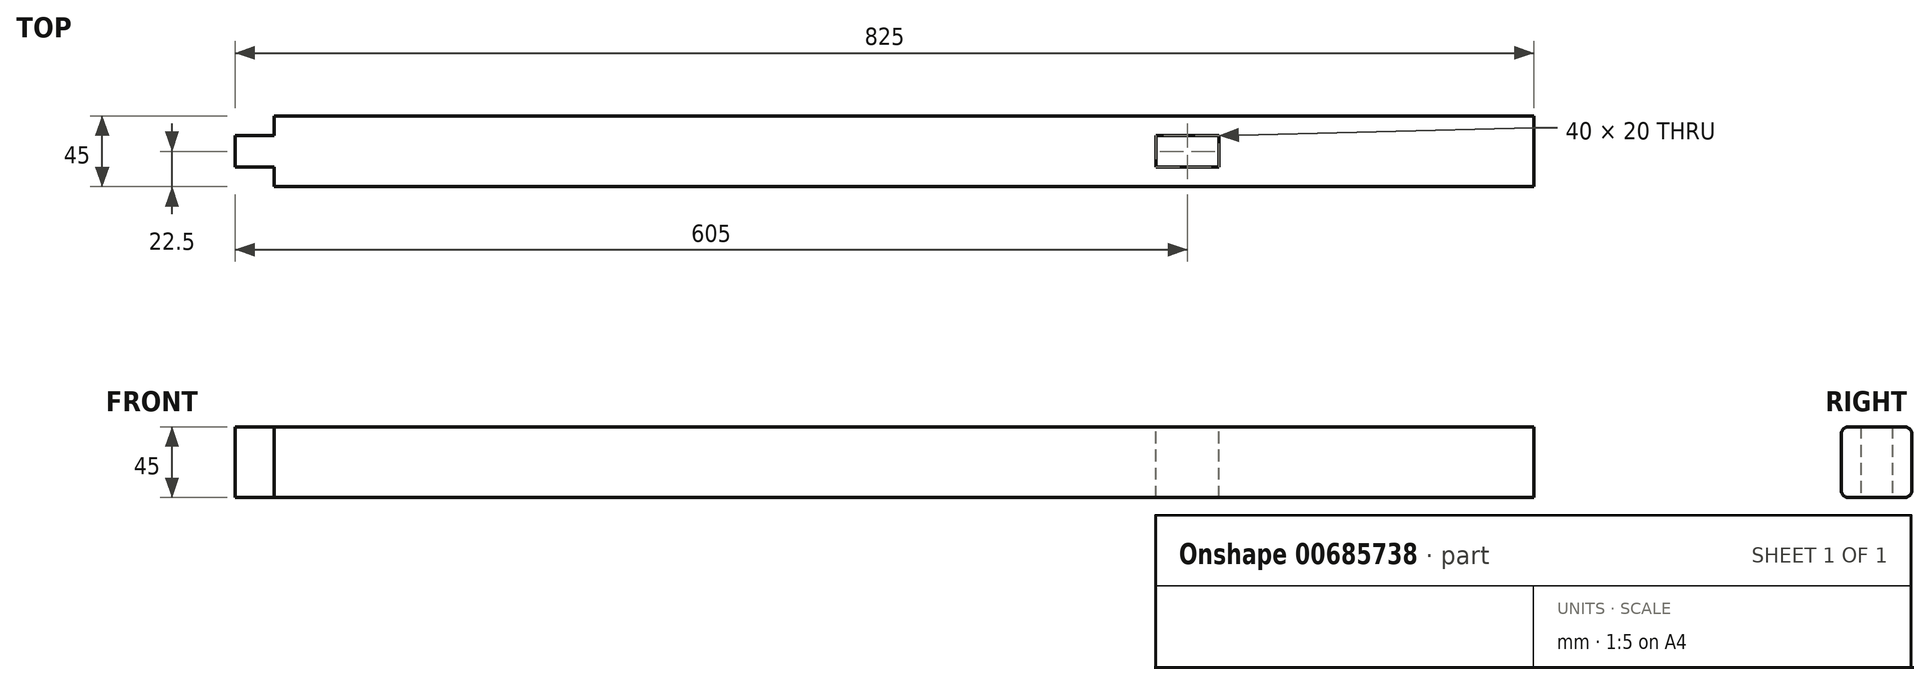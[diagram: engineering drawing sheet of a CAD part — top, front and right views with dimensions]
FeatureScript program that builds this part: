
annotation { "Feature Type Name" : "Feature", "Feature Type Description" : "" }
export const myFeature = defineFeature(function(context is Context, id is Id, definition is map)
    precondition{}
    {
        {
            var Q0;
            Q0=qCreatedBy(makeId("Right.planeOp"),FACE);
            var sketch = newSketch(context, id + "F0", { "sketchPlane" : qUnion([Q0])});
            skLineSegment(sketch, "E0.bottom", {"start": v(22.5, 22.5) * mm, "end": v(-22.5, 22.5) * mm});
            skLineSegment(sketch, "E0.top", {"start": v(22.5, -22.5) * mm, "end": v(-22.5, -22.5) * mm});
            skLineSegment(sketch, "E0.left", {"start": v(22.5, 22.5) * mm, "end": v(22.5, -22.5) * mm});
            skLineSegment(sketch, "E0.right", {"start": v(-22.5, 22.5) * mm, "end": v(-22.5, -22.5) * mm});
            skPoint(sketch, "E0.middle", {"position": v(0, 0) * mm});
            skSolve(sketch);
        }
        {
            var Q0;
            Q0=qSketchRegion(id+"F0",true);
            extrude(context, id + "F1", {"entities" : qUnion([Q0]), "endBound" : BoundingType.SYMMETRIC, "depth" : 800 * mm, "offsetDistance" : 25 * mm});
        }
        {
            var Q0;
            Q0=makeQuery(id+"F1.opExtrude","CAP_FACE",FACE,{"disambiguationData":[OSD([sQuery(id+"F0.wireOp",EDGE,"E0.bottom"),sQuery(id+"F0.wireOp",EDGE,"E0.top"),sQuery(id+"F0.wireOp",EDGE,"E0.left"),sQuery(id+"F0.wireOp",EDGE,"E0.right")])],"isStart":true});
            var sketch = newSketch(context, id + "F2", { "sketchPlane" : qUnion([Q0])});
            skLineSegment(sketch, "E1.bottom", {"start": v(10, 22.5) * mm, "end": v(-10, 22.5) * mm});
            skLineSegment(sketch, "E1.top", {"start": v(10, -22.5) * mm, "end": v(-10, -22.5) * mm});
            skLineSegment(sketch, "E1.left", {"start": v(10, 22.5) * mm, "end": v(10, -22.5) * mm});
            skLineSegment(sketch, "E1.right", {"start": v(-10, 22.5) * mm, "end": v(-10, -22.5) * mm});
            skPoint(sketch, "E1.middle", {"position": v(0, 0) * mm});
            skSolve(sketch);
        }
        {
            var Q0;
            Q0=qSketchRegion(id+"F2",true);
            extrude(context, id + "F3", {"entities" : qUnion([Q0]), "operationType" : NewBodyOperationType.ADD, "depth" : 25 * mm, "offsetDistance" : 25 * mm});
        }
        {
            var Q0;
            Q0=makeQuery(id+"F1.opExtrude","SWEPT_EDGE",EDGE,{"disambiguationData":[OSD([sQuery(id+"F0.wireOp",EDGE,"E0.top"),sQuery(id+"F0.wireOp",EDGE,"E0.right")])]});
            var Q1;
            Q1=makeQuery(id+"F1.opExtrude","SWEPT_EDGE",EDGE,{"disambiguationData":[OSD([sQuery(id+"F0.wireOp",EDGE,"E0.top"),sQuery(id+"F0.wireOp",EDGE,"E0.left")])]});
            var Q2;
            Q2=makeQuery(id+"F1.opExtrude","SWEPT_EDGE",EDGE,{"disambiguationData":[OSD([sQuery(id+"F0.wireOp",EDGE,"E0.bottom"),sQuery(id+"F0.wireOp",EDGE,"E0.right")])]});
            var Q3;
            Q3=makeQuery(id+"F1.opExtrude","SWEPT_EDGE",EDGE,{"disambiguationData":[OSD([sQuery(id+"F0.wireOp",EDGE,"E0.bottom"),sQuery(id+"F0.wireOp",EDGE,"E0.left")])]});
            fillet(context, id + "F4", {"entities" : qUnion([Q0, Q1, Q2, Q3]), "radius" : 5 * mm, "tangentPropagation" : true, "allowEdgeOverflow" : false});
        }
        {
            var Q0;
            Q0=makeQuery(id+"F3.boolean.opBoolean","MERGE",FACE,{"derivedFrom":[makeQuery(id+"F1.opExtrude","SWEPT_FACE",FACE,{"disambiguationData":[OSD([sQuery(id+"F0.wireOp",EDGE,"E0.bottom")])]}),makeQuery(id+"F3.opExtrude","SWEPT_FACE",FACE,{"disambiguationData":[OSD([sQuery(id+"F2.wireOp",EDGE,"E1.bottom")])]})]});
            var sketch = newSketch(context, id + "F5", { "sketchPlane" : qUnion([Q0])});
            skLineSegment(sketch, "E2.bottom", {"start": v(200, 10) * mm, "end": v(160, 10) * mm});
            skLineSegment(sketch, "E2.top", {"start": v(200, -10) * mm, "end": v(160, -10) * mm});
            skLineSegment(sketch, "E2.left", {"start": v(200, 10) * mm, "end": v(200, -10) * mm});
            skLineSegment(sketch, "E2.right", {"start": v(160, 10) * mm, "end": v(160, -10) * mm});
            skPoint(sketch, "E2.middle", {"position": v(180, 0) * mm});
            skSolve(sketch);
        }
        {
            var Q0;
            Q0=qSketchRegion(id+"F5",true);
            extrude(context, id + "F6", {"entities" : qUnion([Q0]), "operationType" : NewBodyOperationType.REMOVE, "endBound" : BoundingType.THROUGH_ALL, "oppositeDirection" : true, "depth" : 25 * mm, "offsetDistance" : 25 * mm});
        }
    });
